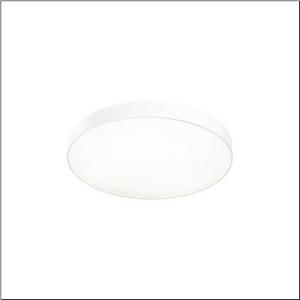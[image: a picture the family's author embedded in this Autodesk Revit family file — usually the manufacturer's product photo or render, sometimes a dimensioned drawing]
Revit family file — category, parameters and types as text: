
# Revit family: round_21_m_51mr36fm8321w
name_source: partatom
category: Lighting Fixtures
units: mm (PartAtom-declared; Revit-internal decimal feet)

## family parameters
Cut with Voids When Loaded = No
Host = Face
Light Source = No
Part Type = Normal
Room Calculation Point = No
Round Connector Dimension = Use Diameter
Shared = No

## types (1)
- --- (1 x LED, 8540 lm, 62.6 W, 3000K)
    Apparent Load = 63 VA
    CIE Flux Codes = 49 80 96 100 100
    Color Rendering = 80
    Color Temperature = 3000K
    Default Elevation = 1800 mm
    Description = Round 21 M, wall and ceiling luminaire, primary optical cover: cover, of PMMA, opal, light emission: direct distribution, primary light characteristic: symmetric, installation type: surface-mounted, suspended mounting, LED, rated luminous flux: 7.700lm, luminous efficacy: 127lm/W, light colour: 830, colour temperature: 3000K, control gear: ON/OFF Multilumen, with terminal, 3-pole, mains connection: 230V, AC, 50/60Hz, rated input power: 61W, housing, of aluminium, coated, white, diameter: 600mm, height: 62mm, protection rating (complete): IP40, insulation class (complete): insulation class I (protective earthing), certification: CE, impact resistance: IK04, permissible operating ambient temperature: -10..+35°C, packaging unit: 1 piece
    Height = 87 mm
    Lamp = 1 x LED
    Lamp Light Flux = 8540 lm
    Lamp Power = 62.6 W
    Lamp count = 1
    Length = 600 mm
    Luminous efficacy = 136 lm/W
    Manufacturer = Siteco
    ModVariant = No
    Model = 51MR36FM8321W
    Mounting Place = Ceiling
    Mounting Type = Surface mounted
    Number of Poles = 1
    OnlyDefault = Yes
    Power Factor = 1
    Product Name = Round 21 M
    Product group = wall and ceiling luminaire
    ProductGroupID = 304
    Protection Class = Protection class I
    Protection Degree = IP 40
    RLX_Detail_Level = 1
    RLX_Emergency_Light_Flux = 0 lm
    RLX_Emergency_Type = 0
    RLX_Emergency_Type_DB = No
    RlxData = <blob elided: 14369 chars, md5=efc76c1e>
    Socket = socket
    Standby Power = 0 W
    System Light Flux = 8540 lm
    System Power = 63 W
    Type Comments = factory setting: luminous flux: 100 % | (ON | ON | ON | ON) | 700 mA
    Type Image = l_1258330.jpg
    URL = http://relux.com
    VarID = @adj_032910
    Voltage = 0 V
    Weight = 0.00 kg
    Width = 0 mm  [stored 0 ft]

note: [stored X ft] marks values corroborated as IEEE doubles in the binary element streams (Revit-internal decimal feet)

## geometry (parser evidence)
native form markers: Sweep x13
no freeform markers — native parametric forms only
